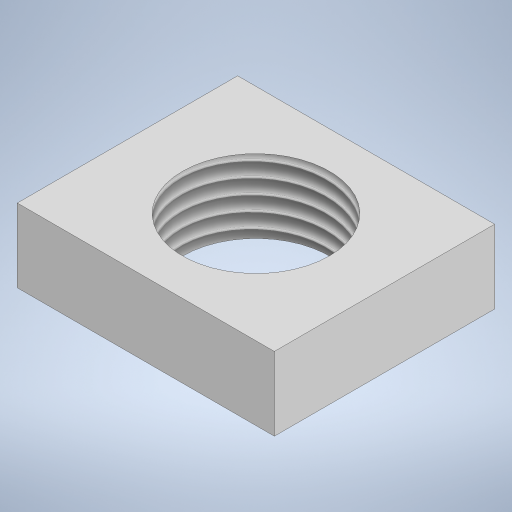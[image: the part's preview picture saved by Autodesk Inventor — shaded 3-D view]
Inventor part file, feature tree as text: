
AUTODESK INVENTOR PART (.ipt)
format: ipt  version: 2023 (Build 270158000, 158)  size: 232,448 bytes
history: native  units: mm
features: other x1, extrude x1, thread x1, sketch x1
ambient origin geometry x8: Origin, YZ Plane, XZ Plane, XY Plane, X Axis, Y Axis, Z Axis, Center Point
bodies: Body1 (feature_tree)
feature tree (4):
  other  "Твердое тело1"
  extrude  "Выдавливание1"  Depth=35.0mm
  thread  "Резьба2"
  sketch  "Эскиз1"
